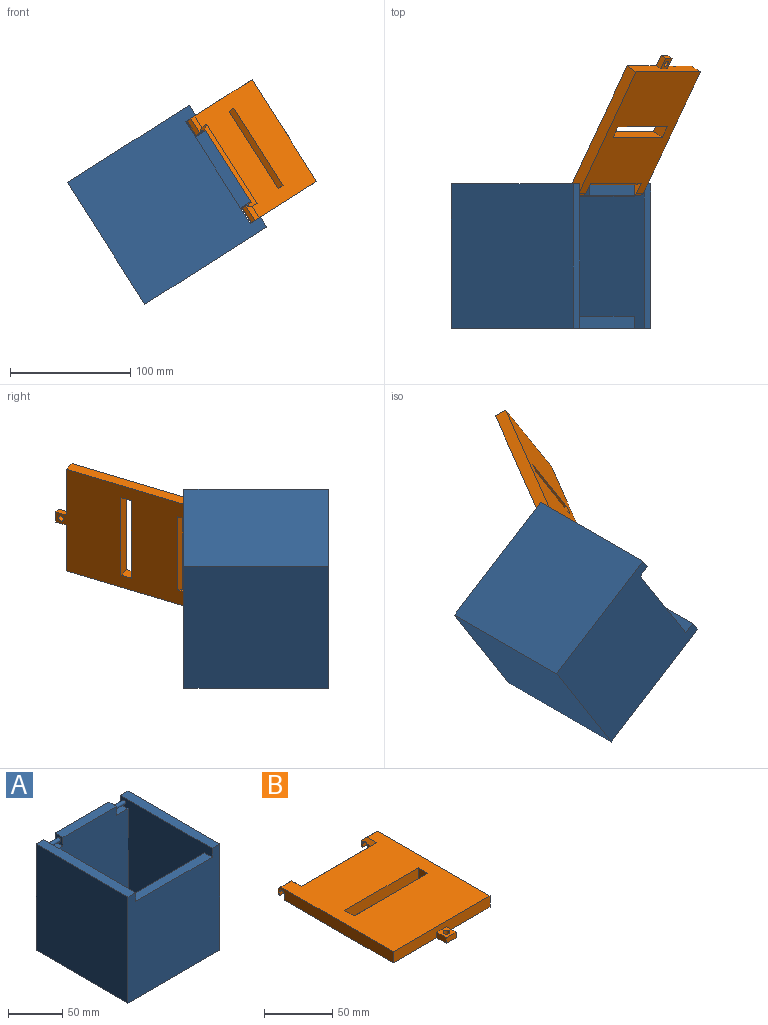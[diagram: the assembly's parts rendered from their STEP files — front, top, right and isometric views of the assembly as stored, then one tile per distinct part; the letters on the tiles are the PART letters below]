
ASSEMBLY  parts=2 mates=1
PART A: 20 faces, bbox 120x120x120 mm
  f0: plane 15x10mm, normal (0,0,1), area 150mm2, adj f2,f6,f7,f15
  f1: plane 120x10mm, normal (0,0,1), area 1200mm2, adj f2,f7,f8,f10
  f2: plane 120x120mm, normal (0,1,0), area 14100mm2, adj f0,f1,f3,f5,f7,f9,f10,f11
  f3: plane 120x120mm, normal (0,0,-1), area 14400mm2, adj f2,f8,f9,f10
  f4: plane 105x100mm, normal (0,1,0), area 10500mm2, adj f5,f7,f12,f14
  f5: plane 120x115mm, normal (-1,0,0), area 11687.4mm2, adj f2,f4,f6,f8,f11,f12,f13,f14
  f6: plane 115x100mm, normal (0,-1,0), area 11200mm2, adj f0,f5,f7,f12,f13,f15,f16,f17
  f7: plane 120x115mm, normal (1,0,0), area 11687.4mm2, adj f0,f1,f2,f4,f6,f8,f12,f14
  f8: plane 120x120mm, normal (0,-1,0), area 13400mm2, adj f1,f3,f5,f7,f9,f10,f11,f14
  f9: plane 120x120mm, normal (1,0,0), area 14400mm2, adj f2,f3,f8,f11
  f10: plane 120x120mm, normal (-1,0,0), area 14400mm2, adj f1,f2,f3,f8
  f11: plane 120x10mm, normal (0,0,1), area 1200mm2, adj f2,f5,f8,f9
  f12: plane 100x100mm, normal (0,0,1), area 10000mm2, adj f4,f5,f6,f7
  f13: plane 15x10mm, normal (0,0,1), area 150mm2, adj f2,f5,f6,f16
  f14: plane 100x10mm, normal (0,0,1), area 1000mm2, adj f4,f5,f7,f8
  f15: plane 10x10mm, normal (-1,0,0), area 87.4mm2, adj f0,f2,f6,f17,f19
  f16: plane 10x10mm, normal (1,0,0), area 87.4mm2, adj f2,f6,f13,f17,f18
  f17: plane 70x10mm, normal (0,0,1), area 700mm2, adj f2,f6,f15,f16
  f18: cylinder r=2mm len=15mm, axis (1,0,0), area 188.5mm2, adj f5,f16
  f19: cylinder r=2mm len=15mm, axis (1,0,0), area 188.5mm2, adj f7,f15
PART B: 35 faces, bbox 100x129x10 mm
  f0: plane 100x10mm, normal (0,-1,0), area 950mm2, adj f1,f2,f12,f13,f30,f31,f32
  f1: plane 116x100mm, normal (0,0,1), area 10058mm2, adj f0,f12,f13,f21,f22,f23,f24,f25
  f2: plane 122.5x100mm, normal (0,0,-1), area 10100.4mm2, adj f0,f3,f10,f11,f12,f13,f16,f20
  f3: plane 7.5x7mm, normal (-1,0,0), area 29.6mm2, adj f2,f8,f10,f17,f20,f24
  f4: plane 5.5x2.5mm, normal (1,0,0), area 7.7mm2, adj f7,f9,f14,f18,f22
  f5: plane 14x4mm, normal (0,1,0), area 56mm2, adj f13,f15,f19,f25
  f6: plane 14x3.44mm, normal (0,-1,0), area 48.1mm2, adj f8,f13,f15,f19
  f7: plane 14x3.44mm, normal (0,-1,0), area 48.1mm2, adj f4,f9,f12,f18
  f8: cylinder r=2.5mm len=14mm, axis (1,0,0), area 109.5mm2, adj f3,f6,f10,f13,f15,f24
  f9: cylinder r=2.5mm len=14mm, axis (1,0,0), area 109.5mm2, adj f4,f7,f11,f12,f16,f22
  f10: plane 14x5.02mm, normal (0,1,0), area 70.3mm2, adj f2,f3,f8,f13
  f11: plane 14x5.02mm, normal (0,1,0), area 70.3mm2, adj f2,f9,f12,f16
  f12: plane 119x10mm, normal (-1,0,0), area 1147.3mm2, adj f0,f1,f2,f7,f9,f11,f14,f18
  f13: plane 119x10mm, normal (1,0,0), area 1147.3mm2, adj f0,f1,f2,f5,f6,f8,f10,f19
  f14: plane 14x4mm, normal (0,1,0), area 56mm2, adj f4,f12,f18,f21
  f15: plane 5.5x2.5mm, normal (-1,0,0), area 7.7mm2, adj f5,f6,f8,f19,f24
  f16: plane 7.5x7mm, normal (1,0,0), area 29.6mm2, adj f2,f9,f11,f17,f20,f22
  f17: plane 72x4mm, normal (0,1,0), area 288mm2, adj f3,f16,f20,f23
  f18: plane 14x1.5mm, normal (0,0.71,-0.71), area 29.7mm2, adj f4,f7,f12,f14
  f19: plane 14x1.5mm, normal (0,0.71,-0.71), area 29.7mm2, adj f5,f6,f13,f15
  f20: plane 72x3mm, normal (0,0.71,-0.71), area 305.5mm2, adj f2,f3,f16,f17
  f21: plane 14x3mm, normal (0,0.71,0.71), area 53mm2, adj f1,f12,f14,f22
  f22: plane 13x3mm, normal (0.71,0,0.71), area 41mm2, adj f1,f4,f9,f16,f21,f23
  f23: plane 78x3mm, normal (0,0.71,0.71), area 318.2mm2, adj f1,f17,f22,f24
  f24: plane 13x3mm, normal (-0.71,0,0.71), area 41mm2, adj f1,f3,f8,f15,f23,f25
  f25: plane 14x3mm, normal (0,0.71,0.71), area 53mm2, adj f1,f5,f13,f24
  f26: plane 76.2x10mm, normal (0,1,0), area 762mm2, adj f1,f2,f27,f29
  f27: plane 10x10mm, normal (-1,0,0), area 100mm2, adj f1,f2,f26,f28
  f28: plane 76.2x10mm, normal (0,-1,0), area 762mm2, adj f1,f2,f27,f29
  f29: plane 10x10mm, normal (1,0,0), area 100mm2, adj f1,f2,f26,f28
  f30: plane 10x5mm, normal (1,0,0), area 50mm2, adj f0,f2,f31,f33
  f31: plane 10x10mm, normal (0,0,1), area 80.4mm2, adj f0,f30,f32,f33,f34
  f32: plane 10x5mm, normal (-1,0,0), area 50mm2, adj f0,f2,f31,f33
  f33: plane 10x5mm, normal (0,-1,0), area 50mm2, adj f2,f30,f31,f32
  f34: cylinder r=2.5mm len=5mm, axis (0,0,1), area 78.5mm2, adj f2,f31
PLACE A rot(axis=(0,1,0),57.6deg) t=(-391.53,-108.11,39.28)mm fixed
PLACE B rot(axis=(0.47,-0.22,0.85),166.1deg) t=(-275.28,-2.19,112.97)mm
MATE cylindrical A.f18 <-> B.f8  axis (0.54,0,-0.84) through (-317.16,-53.11,136.75)mm
